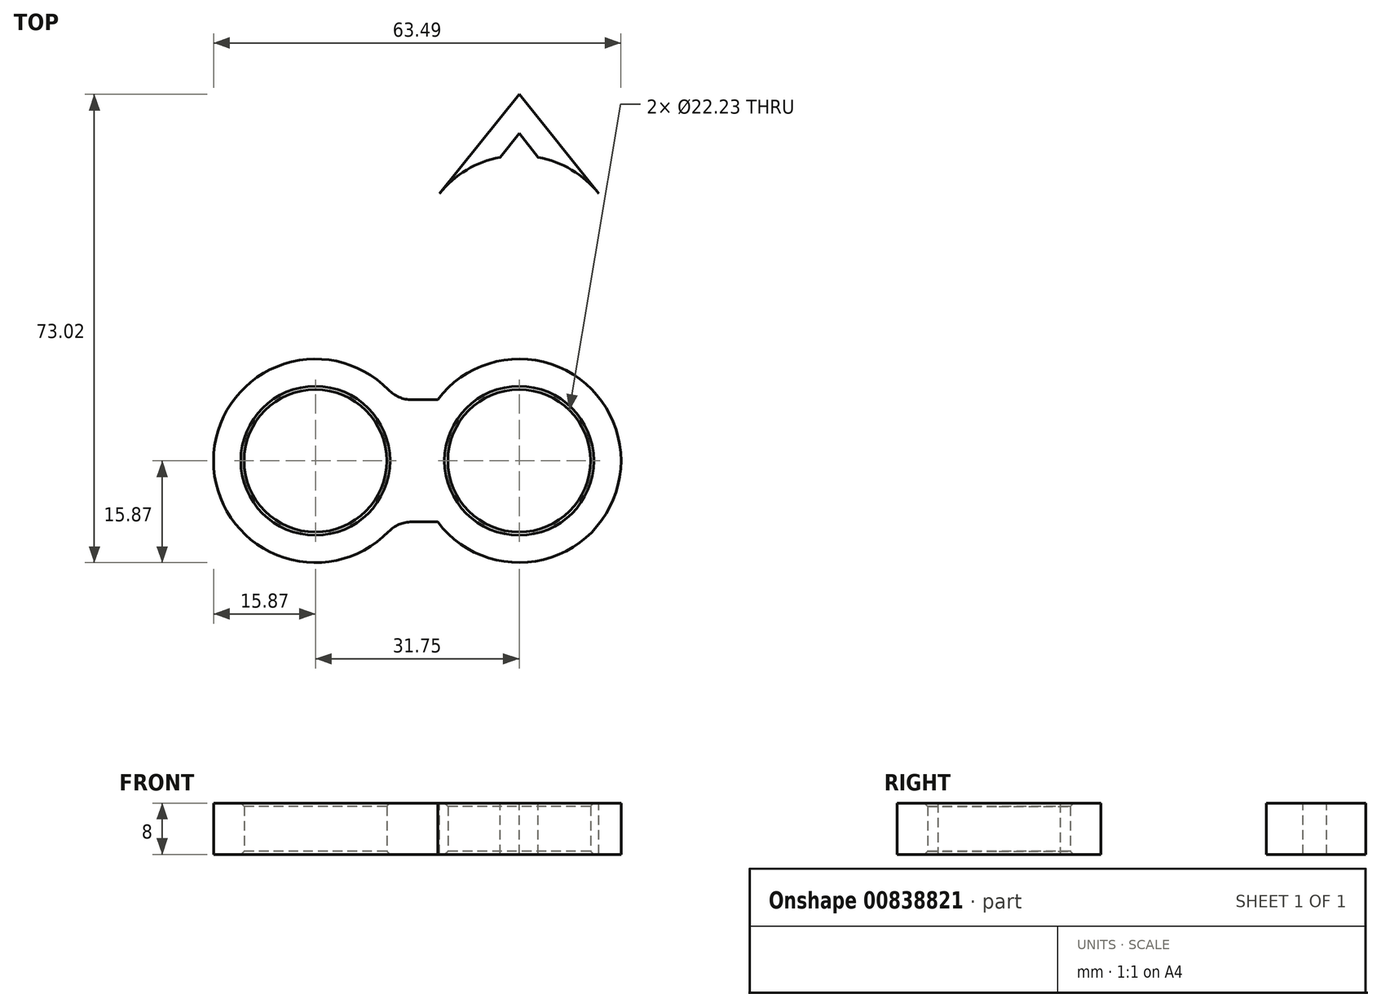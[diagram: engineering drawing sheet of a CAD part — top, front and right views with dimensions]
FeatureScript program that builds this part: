
annotation { "Feature Type Name" : "Feature", "Feature Type Description" : "" }
export const myFeature = defineFeature(function(context is Context, id is Id, definition is map)
    precondition{}
    {
        {
            var Q0;
            Q0=qCreatedBy(makeId("Top.planeOp"),FACE);
            var sketch = newSketch(context, id + "F0", { "sketchPlane" : qUnion([Q0])});
            skCircle(sketch, "E0", {"center": v(0, 0) * mm, "radius": 11.11 * mm});
            skCircle(sketch, "E1", {"center": v(0, 0) * mm, "radius": 15.88 * mm});
            skCircle(sketch, "E2", {"center": v(-31.75, 0) * mm, "radius": 11.11 * mm});
            skCircle(sketch, "E3", {"center": v(-31.75, 0) * mm, "radius": 15.88 * mm});
            skLineSegment(sketch, "E4", {"start": v(-19.05, 9.53) * mm, "end": v(-12.7, 9.53) * mm});
            skLineSegment(sketch, "E5", {"start": v(-12.7, -9.52) * mm, "end": v(-19.05, -9.52) * mm});
            skSolve(sketch);
        }
        {
            var Q0;
            Q0=makeQuery(id+"F0.imprint","IMPRINT",FACE,{"disambiguationData":[TD([[makeQuery(id+"F0.imprint","IMPRINT",EDGE,{"derivedFrom":sQuery(id+"F0.wireOp",EDGE,"E0")}),-1.0]])]});
            var Q1;
            {var subQ0=sQuery(id+"F0.wireOp",EDGE,"E3");var subQ1=sQuery(id+"F0.wireOp",EDGE,"E1");var subQ2=makeQuery(id+"F0.imprint","INTERSECT",VERTEX,{"disambiguationData":[OD(0.0)],"derivedFrom":[subQ1,subQ0]});Q1=makeQuery(id+"F0.imprint","IMPRINT",FACE,{"disambiguationData":[TD([[makeQuery(id+"F0.imprint","IMPRINT",EDGE,{"disambiguationData":[TD([[subQ2,-1.0]])],"derivedFrom":subQ1}),1.0]])]});}
            extrude(context, id + "F1", {"entities" : qUnion([Q0, Q1]), "endBound" : BoundingType.SYMMETRIC, "depth" : 8 * mm, "offsetDistance" : 25.4 * mm});
        }
        {
            var Q0;
            {var subQ0=sQuery(id+"F0.wireOp",EDGE,"E4");Q0=makeQuery(id+"F0.imprint","IMPRINT",FACE,{"disambiguationData":[TD([[makeQuery(id+"F0.imprint","IMPRINT",EDGE,{"derivedFrom":subQ0}),-1.0]])]});}
            var Q1;
            Q1=makeQuery(id+"F0.imprint","IMPRINT",FACE,{"disambiguationData":[TD([[makeQuery(id+"F0.imprint","IMPRINT",EDGE,{"derivedFrom":sQuery(id+"F0.wireOp",EDGE,"E2")}),-1.0]])]});
            var Q2;
            {var subQ0=sQuery(id+"F0.wireOp",EDGE,"E5");Q2=makeQuery(id+"F0.imprint","IMPRINT",FACE,{"disambiguationData":[TD([[makeQuery(id+"F0.imprint","IMPRINT",EDGE,{"derivedFrom":subQ0}),-1.0]])]});}
            extrude(context, id + "F2", {"entities" : qUnion([Q0, Q1, Q2]), "operationType" : NewBodyOperationType.ADD, "endBound" : BoundingType.SYMMETRIC, "depth" : 8 * mm, "offsetDistance" : 25.4 * mm});
        }
        {
            var Q0;
            Q0=makeQuery(id+"FvvAfqHn0FROBtG_1.3.F2.opExtrude","SWEPT_EDGE",EDGE,{"disambiguationData":[OSD([sQuery(id+"F0.wireOp",EDGE,"E1"),sQuery(id+"F0.wireOp",EDGE,"E5")])]});
            var Q1;
            Q1=makeQuery(id+"F2.opExtrude","SWEPT_EDGE",EDGE,{"disambiguationData":[OSD([sQuery(id+"F0.wireOp",EDGE,"E1"),sQuery(id+"F0.wireOp",EDGE,"E4")])]});
            var Q2;
            Q2=makeQuery(id+"F2.opExtrude","SWEPT_EDGE",EDGE,{"disambiguationData":[OSD([sQuery(id+"F0.wireOp",EDGE,"E3"),sQuery(id+"F0.wireOp",EDGE,"E4")])]});
            var Q3;
            Q3=makeQuery(id+"FvvAfqHn0FROBtG_1.3.F2.opExtrude","SWEPT_EDGE",EDGE,{"disambiguationData":[OSD([sQuery(id+"F0.wireOp",EDGE,"E3"),sQuery(id+"F0.wireOp",EDGE,"E5")])]});
            var Q4;
            Q4=makeQuery(id+"F2.opExtrude","SWEPT_EDGE",EDGE,{"disambiguationData":[OSD([sQuery(id+"F0.wireOp",EDGE,"E3"),sQuery(id+"F0.wireOp",EDGE,"E5")])]});
            var Q5;
            Q5=makeQuery(id+"F2.opExtrude","SWEPT_EDGE",EDGE,{"disambiguationData":[OSD([sQuery(id+"F0.wireOp",EDGE,"E1"),sQuery(id+"F0.wireOp",EDGE,"E5")])]});
            var Q6;
            Q6=makeQuery(id+"FvvAfqHn0FROBtG_1.1.F2.opExtrude","SWEPT_EDGE",EDGE,{"disambiguationData":[OSD([sQuery(id+"F0.wireOp",EDGE,"E1"),sQuery(id+"F0.wireOp",EDGE,"E4")])]});
            var Q7;
            Q7=makeQuery(id+"FvvAfqHn0FROBtG_1.1.F2.opExtrude","SWEPT_EDGE",EDGE,{"disambiguationData":[OSD([sQuery(id+"F0.wireOp",EDGE,"E3"),sQuery(id+"F0.wireOp",EDGE,"E4")])]});
            var Q8;
            Q8=makeQuery(id+"FvvAfqHn0FROBtG_1.1.F2.opExtrude","SWEPT_EDGE",EDGE,{"disambiguationData":[OSD([sQuery(id+"F0.wireOp",EDGE,"E3"),sQuery(id+"F0.wireOp",EDGE,"E5")])]});
            var Q9;
            Q9=makeQuery(id+"FvvAfqHn0FROBtG_1.1.F2.opExtrude","SWEPT_EDGE",EDGE,{"disambiguationData":[OSD([sQuery(id+"F0.wireOp",EDGE,"E1"),sQuery(id+"F0.wireOp",EDGE,"E5")])]});
            var Q10;
            Q10=makeQuery(id+"FvvAfqHn0FROBtG_1.2.F2.opExtrude","SWEPT_EDGE",EDGE,{"disambiguationData":[OSD([sQuery(id+"F0.wireOp",EDGE,"E1"),sQuery(id+"F0.wireOp",EDGE,"E4")])]});
            var Q11;
            Q11=makeQuery(id+"FvvAfqHn0FROBtG_1.2.F2.opExtrude","SWEPT_EDGE",EDGE,{"disambiguationData":[OSD([sQuery(id+"F0.wireOp",EDGE,"E3"),sQuery(id+"F0.wireOp",EDGE,"E4")])]});
            var Q12;
            Q12=makeQuery(id+"FvvAfqHn0FROBtG_1.2.F2.opExtrude","SWEPT_EDGE",EDGE,{"disambiguationData":[OSD([sQuery(id+"F0.wireOp",EDGE,"E3"),sQuery(id+"F0.wireOp",EDGE,"E5")])]});
            var Q13;
            Q13=makeQuery(id+"FvvAfqHn0FROBtG_1.2.F2.opExtrude","SWEPT_EDGE",EDGE,{"disambiguationData":[OSD([sQuery(id+"F0.wireOp",EDGE,"E1"),sQuery(id+"F0.wireOp",EDGE,"E5")])]});
            var Q14;
            Q14=makeQuery(id+"FvvAfqHn0FROBtG_1.3.F2.opExtrude","SWEPT_EDGE",EDGE,{"disambiguationData":[OSD([sQuery(id+"F0.wireOp",EDGE,"E1"),sQuery(id+"F0.wireOp",EDGE,"E4")])]});
            var Q15;
            Q15=makeQuery(id+"FvvAfqHn0FROBtG_1.3.F2.opExtrude","SWEPT_EDGE",EDGE,{"disambiguationData":[OSD([sQuery(id+"F0.wireOp",EDGE,"E3"),sQuery(id+"F0.wireOp",EDGE,"E4")])]});
            fillet(context, id + "F3", {"entities" : qUnion([Q0, Q1, Q2, Q3, Q4, Q5, Q6, Q7, Q8, Q9, Q10, Q11, Q12, Q13, Q14, Q15]), "radius" : 5.08 * mm, "tangentPropagation" : true, "allowEdgeOverflow" : false});
        }
        {
            var Q0;
            {var subQ0=sQuery(id+"F0.wireOp",EDGE,"E5");var subQ1=sQuery(id+"F0.wireOp",EDGE,"E4");var subQ2=sQuery(id+"F0.wireOp",EDGE,"E3");var subQ3=sQuery(id+"F0.wireOp",EDGE,"E2");var subQ4=sQuery(id+"F0.wireOp",EDGE,"E1");Q0=makeQuery(id+"FvvAfqHn0FROBtG_1.3.F2.boolean.opBoolean","MERGE",FACE,{"derivedFrom":[makeQuery(id+"FvvAfqHn0FROBtG_1.2.F2.boolean.opBoolean","MERGE",FACE,{"derivedFrom":[makeQuery(id+"FvvAfqHn0FROBtG_1.1.F2.boolean.opBoolean","MERGE",FACE,{"derivedFrom":[makeQuery(id+"F2.boolean.opBoolean","MERGE",FACE,{"derivedFrom":[makeQuery(id+"F1.opExtrude","CAP_FACE",FACE,{"disambiguationData":[OSD([sQuery(id+"F0.wireOp",EDGE,"E0"),subQ4])],"isStart":false}),makeQuery(id+"F2.opExtrude","CAP_FACE",FACE,{"disambiguationData":[OSD([subQ4,subQ3,subQ2,subQ1,subQ0])],"isStart":false})]}),makeQuery(id+"FvvAfqHn0FROBtG_1.1.F2.opExtrude","CAP_FACE",FACE,{"disambiguationData":[OSD([subQ4,subQ3,subQ2,subQ1,subQ0])],"isStart":false})]}),makeQuery(id+"FvvAfqHn0FROBtG_1.2.F2.opExtrude","CAP_FACE",FACE,{"disambiguationData":[OSD([subQ4,subQ3,subQ2,subQ1,subQ0])],"isStart":false})]}),makeQuery(id+"FvvAfqHn0FROBtG_1.3.F2.opExtrude","CAP_FACE",FACE,{"disambiguationData":[OSD([subQ4,subQ3,subQ2,subQ1,subQ0])],"isStart":false})]});}
            var sketch = newSketch(context, id + "F4", { "sketchPlane" : qUnion([Q0])});
            skLineSegment(sketch, "E6", {"start": v(-12.4, 41.67) * mm, "end": v(0, 57.15) * mm});
            skLineSegment(sketch, "E7", {"start": v(0, 57.15) * mm, "end": v(12.4, 41.67) * mm});
            skLineSegment(sketch, "E8", {"start": v(2.97, 47.34) * mm, "end": v(0, 51.05) * mm});
            skLineSegment(sketch, "E9", {"start": v(0, 51.05) * mm, "end": v(-2.97, 47.34) * mm});
            skArc(sketch, "E10.0", {"start": v(11.06, 20.37) * mm, "mid": v(0, 47.62) * mm, "end": v(-11.06, 20.37) * mm});
            skSolve(sketch);
        }
        {
            var Q0;
            {var subQ3=sQuery(id+"F4.wireOp",EDGE,"E6");Q0=makeQuery(id+"F4.imprint","IMPRINT",FACE,{"disambiguationData":[TD([[makeQuery(id+"F4.imprint","IMPRINT",EDGE,{"derivedFrom":subQ3}),-1.0]])]});}
            var Q1;
            {var subQ0=sQuery(id+"F0.wireOp",EDGE,"E5");var subQ1=sQuery(id+"F0.wireOp",EDGE,"E4");var subQ2=sQuery(id+"F0.wireOp",EDGE,"E3");var subQ3=sQuery(id+"F0.wireOp",EDGE,"E2");var subQ4=sQuery(id+"F0.wireOp",EDGE,"E1");Q1=makeQuery(id+"FvvAfqHn0FROBtG_1.3.F2.boolean.opBoolean","MERGE",FACE,{"derivedFrom":[makeQuery(id+"FvvAfqHn0FROBtG_1.2.F2.boolean.opBoolean","MERGE",FACE,{"derivedFrom":[makeQuery(id+"FvvAfqHn0FROBtG_1.1.F2.boolean.opBoolean","MERGE",FACE,{"derivedFrom":[makeQuery(id+"F2.boolean.opBoolean","MERGE",FACE,{"derivedFrom":[makeQuery(id+"F1.opExtrude","CAP_FACE",FACE,{"disambiguationData":[OSD([sQuery(id+"F0.wireOp",EDGE,"E0"),subQ4])],"isStart":true}),makeQuery(id+"F2.opExtrude","CAP_FACE",FACE,{"disambiguationData":[OSD([subQ4,subQ3,subQ2,subQ1,subQ0])],"isStart":true})]}),makeQuery(id+"FvvAfqHn0FROBtG_1.1.F2.opExtrude","CAP_FACE",FACE,{"disambiguationData":[OSD([subQ4,subQ3,subQ2,subQ1,subQ0])],"isStart":true})]}),makeQuery(id+"FvvAfqHn0FROBtG_1.2.F2.opExtrude","CAP_FACE",FACE,{"disambiguationData":[OSD([subQ4,subQ3,subQ2,subQ1,subQ0])],"isStart":true})]}),makeQuery(id+"FvvAfqHn0FROBtG_1.3.F2.opExtrude","CAP_FACE",FACE,{"disambiguationData":[OSD([subQ4,subQ3,subQ2,subQ1,subQ0])],"isStart":true})]});}
            var Q2;
            {var subQ0=sQuery(id+"F0.wireOp",EDGE,"E5");var subQ1=sQuery(id+"F0.wireOp",EDGE,"E4");var subQ2=sQuery(id+"F0.wireOp",EDGE,"E3");var subQ3=sQuery(id+"F0.wireOp",EDGE,"E2");var subQ4=sQuery(id+"F0.wireOp",EDGE,"E1");Q2=makeQuery(id+"FvvAfqHn0FROBtG_1.3.F2.boolean.opBoolean","MERGE",FACE,{"derivedFrom":[makeQuery(id+"FvvAfqHn0FROBtG_1.2.F2.boolean.opBoolean","MERGE",FACE,{"derivedFrom":[makeQuery(id+"FvvAfqHn0FROBtG_1.1.F2.boolean.opBoolean","MERGE",FACE,{"derivedFrom":[makeQuery(id+"F2.boolean.opBoolean","MERGE",FACE,{"derivedFrom":[makeQuery(id+"F1.opExtrude","CAP_FACE",FACE,{"disambiguationData":[OSD([sQuery(id+"F0.wireOp",EDGE,"E0"),subQ4])],"isStart":true}),makeQuery(id+"F2.opExtrude","CAP_FACE",FACE,{"disambiguationData":[OSD([subQ4,subQ3,subQ2,subQ1,subQ0])],"isStart":true})]}),makeQuery(id+"FvvAfqHn0FROBtG_1.1.F2.opExtrude","CAP_FACE",FACE,{"disambiguationData":[OSD([subQ4,subQ3,subQ2,subQ1,subQ0])],"isStart":true})]}),makeQuery(id+"FvvAfqHn0FROBtG_1.2.F2.opExtrude","CAP_FACE",FACE,{"disambiguationData":[OSD([subQ4,subQ3,subQ2,subQ1,subQ0])],"isStart":true})]}),makeQuery(id+"FvvAfqHn0FROBtG_1.3.F2.opExtrude","CAP_FACE",FACE,{"disambiguationData":[OSD([subQ4,subQ3,subQ2,subQ1,subQ0])],"isStart":true})]});}
            extrude(context, id + "F5", {"entities" : qUnion([Q0]), "operationType" : NewBodyOperationType.ADD, "endBound" : BoundingType.UP_TO_SURFACE, "oppositeDirection" : true, "depth" : 7 * mm, "endBoundEntityFace" : qUnion([Q1]), "offsetDistance" : 25.4 * mm});
        }
        {
            var Q0;
            Q0=makeQuery(id+"FvvAfqHn0FROBtG_1.1.F2.opExtrude","CAP_EDGE",EDGE,{"disambiguationData":[OSD([sQuery(id+"F0.wireOp",EDGE,"E2")])],"isStart":false});
            var Q1;
            Q1=makeQuery(id+"F1.opExtrude","CAP_EDGE",EDGE,{"disambiguationData":[OSD([sQuery(id+"F0.wireOp",EDGE,"E0")])],"isStart":false});
            var Q2;
            Q2=makeQuery(id+"F2.opExtrude","CAP_EDGE",EDGE,{"disambiguationData":[OSD([sQuery(id+"F0.wireOp",EDGE,"E2")])],"isStart":false});
            var Q3;
            Q3=makeQuery(id+"FvvAfqHn0FROBtG_1.3.F2.opExtrude","CAP_EDGE",EDGE,{"disambiguationData":[OSD([sQuery(id+"F0.wireOp",EDGE,"E2")])],"isStart":false});
            var Q4;
            Q4=makeQuery(id+"FvvAfqHn0FROBtG_1.2.F2.opExtrude","CAP_EDGE",EDGE,{"disambiguationData":[OSD([sQuery(id+"F0.wireOp",EDGE,"E2")])],"isStart":false});
            var Q5;
            Q5=makeQuery(id+"FvvAfqHn0FROBtG_1.2.F2.opExtrude","CAP_EDGE",EDGE,{"disambiguationData":[OSD([sQuery(id+"F0.wireOp",EDGE,"E2")])],"isStart":true});
            var Q6;
            Q6=makeQuery(id+"FvvAfqHn0FROBtG_1.1.F2.opExtrude","CAP_EDGE",EDGE,{"disambiguationData":[OSD([sQuery(id+"F0.wireOp",EDGE,"E2")])],"isStart":true});
            var Q7;
            Q7=makeQuery(id+"F1.opExtrude","CAP_EDGE",EDGE,{"disambiguationData":[OSD([sQuery(id+"F0.wireOp",EDGE,"E0")])],"isStart":true});
            var Q8;
            Q8=makeQuery(id+"F2.opExtrude","CAP_EDGE",EDGE,{"disambiguationData":[OSD([sQuery(id+"F0.wireOp",EDGE,"E2")])],"isStart":true});
            var Q9;
            Q9=makeQuery(id+"FvvAfqHn0FROBtG_1.3.F2.opExtrude","CAP_EDGE",EDGE,{"disambiguationData":[OSD([sQuery(id+"F0.wireOp",EDGE,"E2")])],"isStart":true});
            chamfer(context, id + "F6", {"entities" : qUnion([Q0, Q1, Q2, Q3, Q4, Q5, Q6, Q7, Q8, Q9]), "width" : 0.5 * mm, "tangentPropagation" : true});
        }
    });
